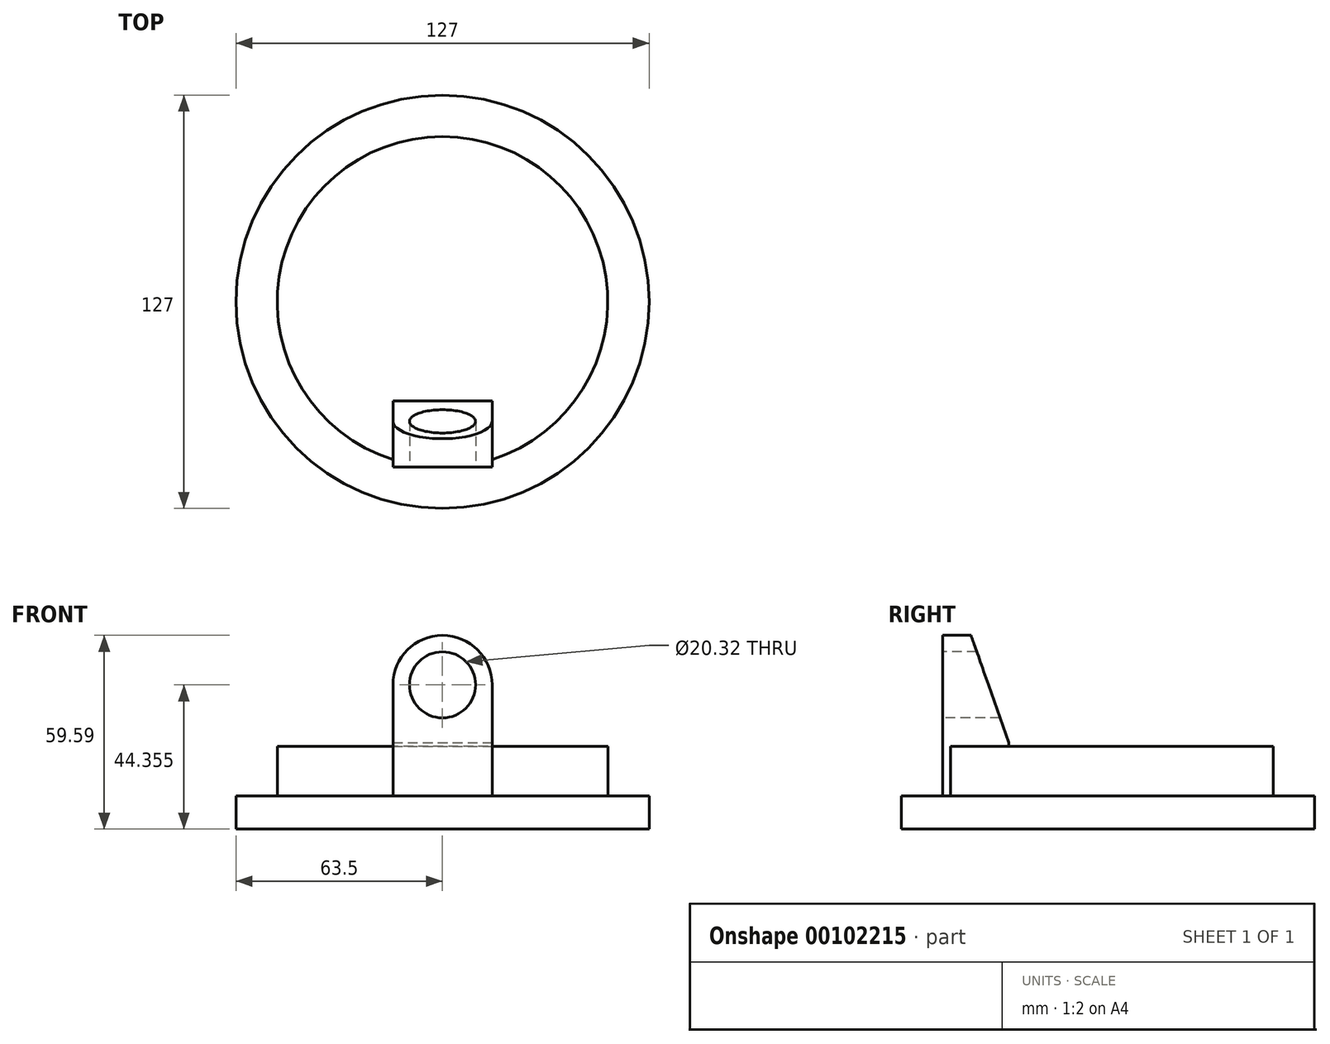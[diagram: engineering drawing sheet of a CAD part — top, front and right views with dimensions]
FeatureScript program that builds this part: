
annotation { "Feature Type Name" : "Feature", "Feature Type Description" : "" }
export const myFeature = defineFeature(function(context is Context, id is Id, definition is map)
    precondition{}
    {
        {
            var Q0;
            Q0=qCreatedBy(makeId("Top.planeOp"),FACE);
            var sketch = newSketch(context, id + "F0", { "sketchPlane" : qUnion([Q0])});
            skCircle(sketch, "E0", {"center": v(0, 0) * mm, "radius": 63.5 * mm});
            skSolve(sketch);
        }
        {
            var Q0;
            Q0=makeQuery(id+"F0.imprint","IMPRINT",FACE,{"disambiguationData":[TD([[makeQuery(id+"F0.imprint","IMPRINT",EDGE,{"derivedFrom":sQuery(id+"F0.wireOp",EDGE,"E0")}),1.0]])]});
            extrude(context, id + "F1", {"entities" : qUnion([Q0]), "oppositeDirection" : true, "depth" : 10.16 * mm});
        }
        {
            var Q0;
            Q0=makeQuery(id+"F1.opExtrude","CAP_FACE",FACE,{"disambiguationData":[OSD([sQuery(id+"F0.wireOp",EDGE,"E0")])],"isStart":true});
            var sketch = newSketch(context, id + "F2", { "sketchPlane" : qUnion([Q0])});
            skCircle(sketch, "E1", {"center": v(0, 0) * mm, "radius": 50.8 * mm});
            skSolve(sketch);
        }
        {
            var Q0;
            Q0=makeQuery(id+"F2.imprint","IMPRINT",FACE,{"disambiguationData":[TD([[makeQuery(id+"F2.imprint","IMPRINT",EDGE,{"derivedFrom":sQuery(id+"F2.wireOp",EDGE,"E1")}),1.0]])]});
            extrude(context, id + "F3", {"entities" : qUnion([Q0]), "operationType" : NewBodyOperationType.ADD, "depth" : 15.24 * mm});
        }
        {
            var Q0;
            Q0=qCreatedBy(makeId("Front.planeOp"),FACE);
            cPlane(context, id + "F4", {"entities" : qUnion([Q0]), "cplaneType" : CPlaneType.OFFSET, "offset" : 50.8 * mm, "width" : 152.4 * mm, "height" : 152.4 * mm});
        }
        {
            var Q0;
            Q0=qCreatedBy(id+"F4.planeOp",FACE);
            var sketch = newSketch(context, id + "F5", { "sketchPlane" : qUnion([Q0])});
            skLineSegment(sketch, "E2.top", {"start": v(-15.24, 0) * mm, "end": v(15.24, 0) * mm});
            skLineSegment(sketch, "E2.left", {"start": v(-15.24, 34.2) * mm, "end": v(-15.24, 0) * mm});
            skLineSegment(sketch, "E2.right", {"start": v(15.24, 34.2) * mm, "end": v(15.24, 0) * mm});
            skPoint(sketch, "E2.middle", {"position": v(0, 23.04) * mm});
            skPoint(sketch, "E3.orphan", {"position": v(-15.24, 46.09) * mm});
            skPoint(sketch, "E4.orphan", {"position": v(15.24, 46.09) * mm});
            skArc(sketch, "E5", {"start": v(15.24, 34.2) * mm, "mid": v(0, 49.43) * mm, "end": v(-15.24, 34.2) * mm});
            skSolve(sketch);
        }
        {
            var Q0;
            Q0=makeQuery(id+"F5.imprint","IMPRINT",FACE,{"disambiguationData":[TD([[makeQuery(id+"F5.imprint","IMPRINT",EDGE,{"derivedFrom":sQuery(id+"F5.wireOp",EDGE,"E2.top")}),1.0]])]});
            extrude(context, id + "F6", {"entities" : qUnion([Q0]), "operationType" : NewBodyOperationType.ADD, "oppositeDirection" : true, "depth" : 20.32 * mm});
        }
        {
            var Q0;
            Q0=makeQuery(id+"F6.opExtrude","CAP_FACE",FACE,{"disambiguationData":[OSD([sQuery(id+"F5.wireOp",EDGE,"E2.top"),sQuery(id+"F5.wireOp",EDGE,"E2.left"),sQuery(id+"F5.wireOp",EDGE,"E2.right"),sQuery(id+"F5.wireOp",EDGE,"E5")])],"isStart":true});
            var sketch = newSketch(context, id + "F7", { "sketchPlane" : qUnion([Q0])});
            skCircle(sketch, "E6", {"center": v(0, 34.2) * mm, "radius": 10.16 * mm});
            skSolve(sketch);
        }
        {
            var Q0;
            Q0=makeQuery(id+"F7.imprint","IMPRINT",FACE,{"disambiguationData":[TD([[makeQuery(id+"F7.imprint","IMPRINT",EDGE,{"derivedFrom":sQuery(id+"F7.wireOp",EDGE,"E6")}),1.0]])]});
            extrude(context, id + "F8", {"entities" : qUnion([Q0]), "operationType" : NewBodyOperationType.REMOVE, "oppositeDirection" : true, "depth" : 25.4 * mm});
        }
        {
            var Q0;
            Q0=qCreatedBy(makeId("Right.planeOp"),FACE);
            cPlane(context, id + "F9", {"entities" : qUnion([Q0]), "cplaneType" : CPlaneType.OFFSET, "offset" : 15.24 * mm, "width" : 152.4 * mm, "height" : 152.4 * mm});
        }
        {
            var Q0;
            Q0=qCreatedBy(id+"F9.planeOp",FACE);
            var sketch = newSketch(context, id + "F10", { "sketchPlane" : qUnion([Q0])});
            skLineSegment(sketch, "E7", {"start": v(-42.6, 50.79) * mm, "end": v(-30.17, 15.56) * mm});
            skLineSegment(sketch, "E8", {"start": v(-30.17, 15.56) * mm, "end": v(-30.17, 50.79) * mm});
            skLineSegment(sketch, "E9", {"start": v(-30.17, 50.79) * mm, "end": v(-42.6, 50.79) * mm});
            skSolve(sketch);
        }
        {
            var Q0;
            Q0=makeQuery(id+"F10.imprint","IMPRINT",FACE,{"disambiguationData":[TD([[makeQuery(id+"F10.imprint","IMPRINT",EDGE,{"derivedFrom":sQuery(id+"F10.wireOp",EDGE,"E7")}),1.0]])]});
            extrude(context, id + "F11", {"entities" : qUnion([Q0]), "operationType" : NewBodyOperationType.REMOVE, "oppositeDirection" : true, "depth" : 30.48 * mm});
        }
    });
